# Revit family: York CBAL2-24 Wide, Linear Chilled Beam, Face Hosted, Revit 2020, R1.7
name_source: partatom
category: Mechanical Equipment
units: mm (PartAtom-declared; Revit-internal decimal feet)

## family parameters
Cut with Voids When Loaded = Yes
Host = Face
OmniClass Number = 23.75.70.17.31
OmniClass Title = Induction Units
Part Type = Normal
Room Calculation Point = No
Round Connector Dimension = Use Radius
Shared = No

## types (2) — shared parameters
0 - No Insulation = Yes
10 Feet = No
10" Oval = No
2 Feet = Yes
24" Wide Beam = Yes
26 - White = Yes
2P2C - 2-Pipe, 2 Coil Circuit = No
3 - LAY-IN = No
3 Feet = No
3PT - 3/4" Male Pipe Thread = No
4 Feet = No
4" Dia. = Yes
4P2C - 4-Pipe, 2 Coil Circuit = No
5 Feet = No
5" Dia. = No
6 Feet = No
6" Dia. = No
7 Feet = No
8 Feet = No
8" Oval = No
84 - Black = No
9 Feet = No
Actual Cooling Entering Dry Bulb Temperature = 0 °F
Actual Cooling Entering Wet Bulb Temperature = 0 °F
Actual Cooling Leaving Dry Bulb Temperature = 0 °F
Actual Cooling Leaving Wet Bulb Temperature = 0 °F
Actual External Static Pressure = 0.00 in-wg
Actual Heating Entering Dry Bulb Temperature = 0 °F
Actual Heating Leaving Dry Bulb Temperature = 0 °F
Actual Height = 8 3/8"
Actual Oval Width = 9 3/8"
Actual Oval height = 5 1/4"
Actual Radius = 1 15/16"
Actual Total Static Pressure = 0.00 in-wg
Air-Flow Direction Label Visibility = Yes
Arrow text w = 5 3/4"
Arrow text w2 = 6 3/4"
B - One-way, Back = No
CTL Cleance box H1 = 23 1/2"
CTRL Angle = 90.00°
CTRL Multi-Inlet Angle = 90.00°
CTRL Multi-Inlet Connector Offset = 8 1/2"
CTRL Multi-Inlet Offset = 0"
CTRL Multi-Inlet Oval Angle = 0.00°
CTRL Multi-Inlet Oval Connector Offset = 6 5/64"
CTRL Multi-Inlet Round Angle = 90.00°
CTRL Multi-Inlet Round Connector Offset = 8 1/2"
CTRL Offset = 7/16"
CTRL Oval Connector Offset = 4"
CTRL Perforation Hole Dia = 1/8"
CTRL Perforation Offset = 1/2"
CTRL Round Connector Offset = 0"
CTRL Thickness = 1/16"
CWR Outlet Description = CWR-Outlet
CWR Ver Offset = 7"
CWS Inlet Description = CWS Inlet
CWS Ver Offset = 7 5/8"
Clearance Material = Clearance Material
Coil Material = Metal - Copper
Condenser Inlet Radius = 1/4"
Condenser Outlet Radius = 1/4"
Condenser Pressure Drop = 0.00 psi
Conditioned Air (Oval) Description = Disabled
Conditioned Air (Round) Description = Conditioned Air
Conditioned Air Connection Height = 1/2"
Conditioned Air Connection Radius = 2"
Conditioned Air Connection Width = 1/2"
Connector Offset = 6 5/64"
Default Elevation = 0"
Description = Linear Chilled Beam Diffuser, Ceiling Mounted
Design Ambient Summer Dry Bulb Temperature = 0 °F
Design Ambient Winter Dry Bulb Temperature = 0 °F
Design Ambient summer Wet bulb Temperature = 0 °F
Design Cooling Minimum Air Flow = 0 CFM
Design Heating Maximum Air Flow = 0 CFM
Design Heating Minimum Air Flow = 0 CFM
Design cooling Maximum Air Flow = 0 CFM
Evaporator Inlet Radius = 1/4"
Evaporator Outlet Radius = 1/4"
Evaporator Pressure Drop = 0.00 psi
F = 4 1/2"
Frame Extension = 3/8"
Front Arrow = Yes
G = 4"
H12 - SS Flex Hose - 12in = No
H18 - SS Flex Hose - 18in = No
H24 - SS Flex Hose - 24in = No
HWR Description = HWR Outlet
HWS Inlet Description = HWS Inlet
Hanger Dimension F = 4 5/16"
Hanger Visibility = No
Height = 10 1/8"
Hor Chilled Water Return Offset = 7 1/8"
Hor Chilled Water Supply Offset = 7 3/4"
Hor Hot Water Return Offset = 2 1/2"
Hor Hot Water Supply Offset = 2 1/2"
Inner Length = 23"
Inner Width = 23 3/8"
Input your Special Finish's name = Input your Special Finish's name
L - ½” EcoShield (Foil Face) = No
Lay In Width = 23 3/4"
Layin depath = 3/8"
M13 = Yes
M17 = No
M19 = No
M23 = No
M27 = No
M31 = No
MPT - 1/2" Male Pipe Thread = No
Manufacturer = York Inc
Material = Galvanized G90
Model = CB-AL2-YK-24
Multi-Inlet = Yes
NT - Tegular 9/16 Inch = Yes
Pipe Height = 6"
Primary Air Extension = 2 5/8"
Primary Air Ver Offset = 6 1/8"
SWT - Sweat = Yes
Select Border Type = 2
Select a Beam Length = 1
Select a Piping Connection Type = 1
Select an Air Inlet Dia = 1
Select an Air Nozzle Configuration = 1
Select an Exposed Face Finish = 1
Select an Outside Liner = ***************  Insulation ************
Show Clearance Box = No
Show Oval Connector = No
Show Room Tag = No
Show Round Connector = Yes
Side Middle = No
Side Plate = Yes
Top Middle = No
Top Plate = Yes
Total Length = 23 3/8"
Total Width = 23 3/8"
URL = https://www.york.com
zero-valued in all types: Actual Coefficient of Performance, Actual Energy Efficiency Rating (BTU/h.W), Actual Filter Face Area, Actual Full Load Efficiency

## per-type parameters (varying)
| type | 2 - Two-way,Throw | 2-Pipe System | 2P1C - 2-Pipe, 1 Coil Circuit | 4-Pipe System | 4P1C - 4-Pipe, 1 Coil Circuit | Back Arrow | CTRL Clearance Box Width1 | CTRL Pipe Connector Offset | F - One-way, Front | HWR Ver Offset | HWS Ver Offset | Left Hand Side | Right Hand Side | Select a Water Coil Connection | Select a Water-Coil Type | Select an Air Inlet Location | Select an Air Throw Pattern |
| CB-AL2-YK -24-LAY-IN | Yes | Yes | Yes | No | No | Yes | 36" | 1 43/64" | No | 7" | 7 5/8" | Yes | No | 1 | 1 | 3 | 1 |
| CB-AL2-YK-24 NT Border Type | No | No | No | Yes | Yes | No | 23 1/2" | 21 45/64" | Yes | 9 1/2" | 10 1/8" | No | Yes | 2 | 2 | 4 | 2 |

## geometry (parser evidence)
native form markers: Sweep x37
no freeform markers — native parametric forms only
